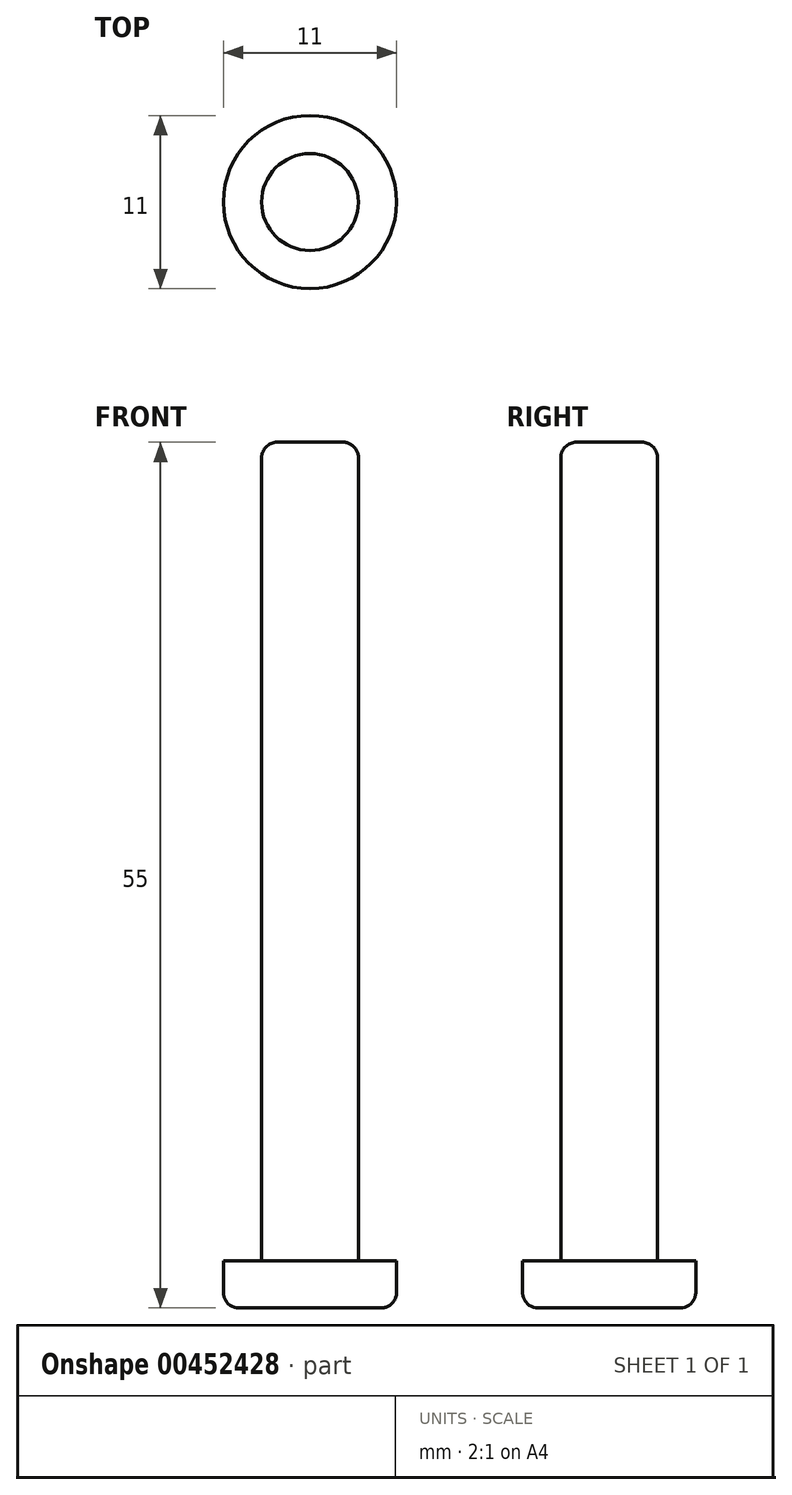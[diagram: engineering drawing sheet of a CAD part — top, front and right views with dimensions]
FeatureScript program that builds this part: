
annotation { "Feature Type Name" : "Feature", "Feature Type Description" : "" }
export const myFeature = defineFeature(function(context is Context, id is Id, definition is map)
    precondition{}
    {
        {
            var Q0;
            Q0=qCreatedBy(makeId("Top.planeOp"),FACE);
            var sketch = newSketch(context, id + "F0", { "sketchPlane" : qUnion([Q0])});
            skCircle(sketch, "E0", {"center": v(0, 0) * mm, "radius": 5.5 * mm});
            skSolve(sketch);
        }
        {
            var Q0;
            Q0=makeQuery(id+"F0.imprint","IMPRINT",FACE,{"disambiguationData":[TD([[makeQuery(id+"F0.imprint","IMPRINT",EDGE,{"derivedFrom":sQuery(id+"F0.wireOp",EDGE,"E0")}),1.0]])]});
            extrude(context, id + "F1", {"entities" : qUnion([Q0]), "depth" : 3 * mm, "offsetDistance" : 25 * mm});
        }
        {
            var Q0;
            Q0=makeQuery(id+"F1.opExtrude","CAP_FACE",FACE,{"disambiguationData":[OSD([sQuery(id+"F0.wireOp",EDGE,"E0")])],"isStart":false});
            var sketch = newSketch(context, id + "F2", { "sketchPlane" : qUnion([Q0])});
            skCircle(sketch, "E1", {"center": v(0, 0) * mm, "radius": 3.08 * mm});
            skSolve(sketch);
        }
        {
            var Q0;
            Q0=makeQuery(id+"F2.imprint","IMPRINT",FACE,{"disambiguationData":[TD([[makeQuery(id+"F2.imprint","IMPRINT",EDGE,{"derivedFrom":sQuery(id+"F2.wireOp",EDGE,"E1")}),1.0]])]});
            extrude(context, id + "F3", {"entities" : qUnion([Q0]), "operationType" : NewBodyOperationType.ADD, "depth" : 52 * mm, "offsetDistance" : 25 * mm});
        }
        {
            var Q0;
            Q0=makeQuery(id+"F3.opExtrude","CAP_EDGE",EDGE,{"disambiguationData":[OSD([sQuery(id+"F2.wireOp",EDGE,"E1")])],"isStart":false});
            var Q1;
            Q1=makeQuery(id+"F1.opExtrude","CAP_EDGE",EDGE,{"disambiguationData":[OSD([sQuery(id+"F0.wireOp",EDGE,"E0")])],"isStart":true});
            fillet(context, id + "F4", {"entities" : qUnion([Q0, Q1]), "radius" : 1 * mm, "tangentPropagation" : true, "allowEdgeOverflow" : false});
        }
    });
